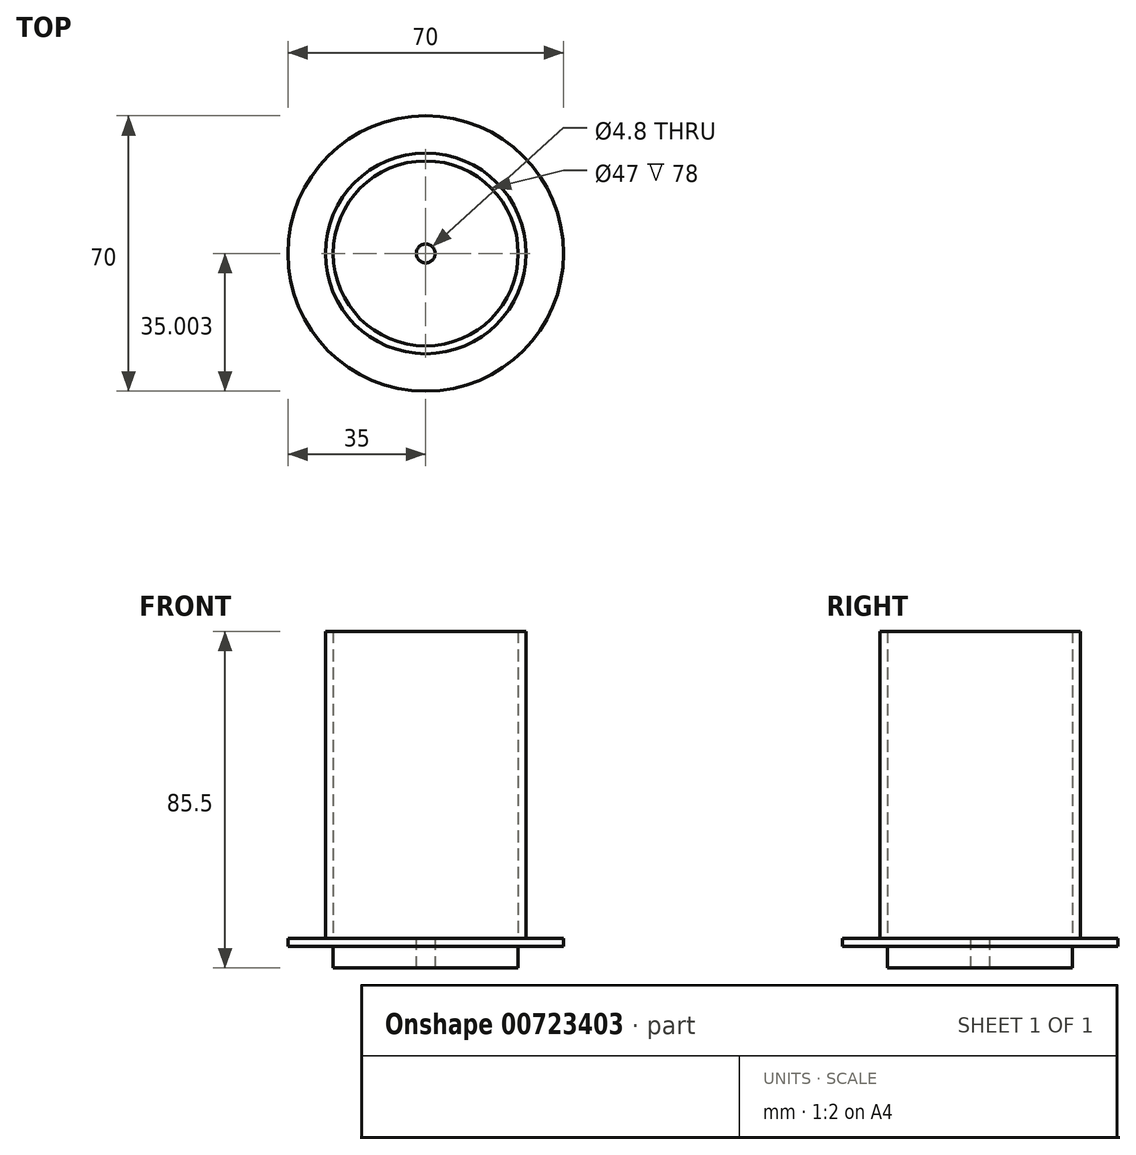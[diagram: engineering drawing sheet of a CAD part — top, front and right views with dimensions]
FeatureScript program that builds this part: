
annotation { "Feature Type Name" : "Feature", "Feature Type Description" : "" }
export const myFeature = defineFeature(function(context is Context, id is Id, definition is map)
    precondition{}
    {
        {
            var Q0;
            Q0=qCreatedBy(makeId("Top.planeOp"),FACE);
            var sketch = newSketch(context, id + "F0", { "sketchPlane" : qUnion([Q0])});
            skArc(sketch, "E0", {"start": v(20.08, -12.5) * mm, "mid": v(24.36, 1.65) * mm, "end": v(20.08, 15.8) * mm});
            skLineSegment(sketch, "E1.left", {"start": v(-10.34, -1.25) * mm, "end": v(-10.34, 4.55) * mm});
            skLineSegment(sketch, "E1.right", {"start": v(-5.54, -0.85) * mm, "end": v(-5.54, 4.15) * mm});
            skLineSegment(sketch, "E2", {"start": v(-10.34, 4.55) * mm, "end": v(-8.34, 4.55) * mm});
            skLineSegment(sketch, "E3", {"start": v(-8.34, 4.55) * mm, "end": v(-8.34, 6.55) * mm});
            skLineSegment(sketch, "E4", {"start": v(-8.34, 6.55) * mm, "end": v(-7.34, 6.55) * mm});
            skLineSegment(sketch, "E5", {"start": v(-7.34, 6.55) * mm, "end": v(-5.54, 4.15) * mm});
            skLineSegment(sketch, "E6", {"start": v(-10.34, -1.25) * mm, "end": v(-8.34, -1.25) * mm});
            skLineSegment(sketch, "E7", {"start": v(-8.34, -1.25) * mm, "end": v(-8.34, -3.25) * mm});
            skLineSegment(sketch, "E8", {"start": v(-8.34, -3.25) * mm, "end": v(-7.34, -3.25) * mm});
            skLineSegment(sketch, "E9", {"start": v(-7.34, -3.25) * mm, "end": v(-5.54, -0.85) * mm});
            skCircle(sketch, "E10", {"center": v(-1.14, 1.65) * mm, "radius": 35 * mm});
            skArc(sketch, "E11.0", {"start": v(18.63, -11.05) * mm, "mid": v(22.36, 1.65) * mm, "end": v(18.63, 14.35) * mm});
            skLineSegment(sketch, "E12.bottom", {"start": v(-15.29, 22.87) * mm, "end": v(-13.84, 21.42) * mm});
            skLineSegment(sketch, "E12.top", {"start": v(-22.36, 15.8) * mm, "end": v(-20.91, 14.35) * mm});
            skLineSegment(sketch, "E13.MirrorCS", {"start": v(20.08, 15.8) * mm, "end": v(18.63, 14.35) * mm});
            skLineSegment(sketch, "E14.MirrorCS", {"start": v(13, 22.87) * mm, "end": v(11.56, 21.42) * mm});
            skLineSegment(sketch, "E15.trimOffspring", {"start": v(11.56, -18.12) * mm, "end": v(13, -19.56) * mm});
            skLineSegment(sketch, "E16.trimOffspring", {"start": v(-13.84, -18.12) * mm, "end": v(-15.29, -19.56) * mm});
            skLineSegment(sketch, "E17.trimOffspring", {"start": v(-20.91, -11.05) * mm, "end": v(-22.36, -12.5) * mm});
            skLineSegment(sketch, "E18.trimOffspring", {"start": v(18.63, -11.05) * mm, "end": v(20.08, -12.5) * mm});
            skArc(sketch, "E19.trimOffspring", {"start": v(13, 22.87) * mm, "mid": v(-1.14, 27.15) * mm, "end": v(-15.29, 22.87) * mm});
            skArc(sketch, "E20.trimOffspring", {"start": v(11.56, 21.42) * mm, "mid": v(-1.14, 25.15) * mm, "end": v(-13.84, 21.42) * mm});
            skArc(sketch, "E21.trimOffspring", {"start": v(-20.91, 14.35) * mm, "mid": v(-24.64, 1.65) * mm, "end": v(-20.91, -11.05) * mm});
            skArc(sketch, "E22.trimOffspring", {"start": v(-22.36, 15.8) * mm, "mid": v(-26.64, 1.65) * mm, "end": v(-22.36, -12.5) * mm});
            skArc(sketch, "E23.trimOffspring", {"start": v(-13.84, -18.12) * mm, "mid": v(-1.14, -21.85) * mm, "end": v(11.56, -18.12) * mm});
            skArc(sketch, "E24.trimOffspring", {"start": v(-15.29, -19.56) * mm, "mid": v(-1.14, -23.85) * mm, "end": v(13, -19.56) * mm});
            skLineSegment(sketch, "E25.MirrorCS", {"start": v(3.26, -0.85) * mm, "end": v(3.26, 4.15) * mm});
            skLineSegment(sketch, "E26.MirrorCS", {"start": v(5.06, 6.55) * mm, "end": v(3.26, 4.15) * mm});
            skLineSegment(sketch, "E27.MirrorCS", {"start": v(6.06, 6.55) * mm, "end": v(5.06, 6.55) * mm});
            skLineSegment(sketch, "E28.MirrorCS", {"start": v(6.06, 4.55) * mm, "end": v(6.06, 6.55) * mm});
            skLineSegment(sketch, "E29.MirrorCS", {"start": v(8.06, 4.55) * mm, "end": v(6.06, 4.55) * mm});
            skLineSegment(sketch, "E30.MirrorCS", {"start": v(8.06, -1.25) * mm, "end": v(8.06, 4.55) * mm});
            skLineSegment(sketch, "E31.MirrorCS", {"start": v(8.06, -1.25) * mm, "end": v(6.06, -1.25) * mm});
            skLineSegment(sketch, "E32.MirrorCS", {"start": v(6.06, -1.25) * mm, "end": v(6.06, -3.25) * mm});
            skLineSegment(sketch, "E33.MirrorCS", {"start": v(6.06, -3.25) * mm, "end": v(5.06, -3.25) * mm});
            skLineSegment(sketch, "E34.MirrorCS", {"start": v(5.06, -3.25) * mm, "end": v(3.26, -0.85) * mm});
            skLineSegment(sketch, "E35.0", {"start": v(-55.8, 19.45) * mm, "end": v(-55.8, 19.45) * mm});
            skLineSegment(sketch, "E36.MirrorCS", {"start": v(1.76, -7.55) * mm, "end": v(1.76, -5.55) * mm});
            skLineSegment(sketch, "E37.MirrorCS", {"start": v(-6.04, -5.55) * mm, "end": v(-6.04, -4.55) * mm});
            skLineSegment(sketch, "E38.MirrorCS", {"start": v(-4.04, -7.55) * mm, "end": v(-4.04, -5.55) * mm});
            skLineSegment(sketch, "E39.MirrorCS", {"start": v(3.76, -5.55) * mm, "end": v(3.76, -4.55) * mm});
            skLineSegment(sketch, "E40.MirrorCS", {"start": v(3.76, -4.55) * mm, "end": v(1.36, -2.75) * mm});
            skLineSegment(sketch, "E41.MirrorCS", {"start": v(1.76, -5.55) * mm, "end": v(3.76, -5.55) * mm});
            skLineSegment(sketch, "E42.MirrorCS", {"start": v(-4.04, -5.55) * mm, "end": v(-6.04, -5.55) * mm});
            skLineSegment(sketch, "E43.MirrorCS", {"start": v(1.76, -7.55) * mm, "end": v(-4.04, -7.55) * mm});
            skLineSegment(sketch, "E44.MirrorCS", {"start": v(1.36, -2.75) * mm, "end": v(-3.64, -2.75) * mm});
            skLineSegment(sketch, "E45.MirrorCS", {"start": v(-6.04, -4.55) * mm, "end": v(-3.64, -2.75) * mm});
            skLineSegment(sketch, "E46.MirrorCS", {"start": v(3.76, 8.85) * mm, "end": v(3.76, 7.85) * mm});
            skLineSegment(sketch, "E47.MirrorCS", {"start": v(-4.04, 10.85) * mm, "end": v(-4.04, 8.85) * mm});
            skLineSegment(sketch, "E48.MirrorCS", {"start": v(-6.04, 7.85) * mm, "end": v(-3.64, 6.05) * mm});
            skLineSegment(sketch, "E49.MirrorCS", {"start": v(1.76, 10.85) * mm, "end": v(-4.04, 10.85) * mm});
            skLineSegment(sketch, "E50.MirrorCS", {"start": v(1.36, 6.05) * mm, "end": v(-3.64, 6.05) * mm});
            skLineSegment(sketch, "E51.MirrorCS", {"start": v(3.76, 7.85) * mm, "end": v(1.36, 6.05) * mm});
            skLineSegment(sketch, "E52.MirrorCS", {"start": v(1.76, 10.85) * mm, "end": v(1.76, 8.85) * mm});
            skLineSegment(sketch, "E53.MirrorCS", {"start": v(-4.04, 8.85) * mm, "end": v(-6.04, 8.85) * mm});
            skCircle(sketch, "E54.MirrorC", {"center": v(-1.14, 1.65) * mm, "radius": 2.4 * mm});
            skLineSegment(sketch, "E55.MirrorCS", {"start": v(-6.04, 8.85) * mm, "end": v(-6.04, 7.85) * mm});
            skLineSegment(sketch, "E56.MirrorCS", {"start": v(1.76, 8.85) * mm, "end": v(3.76, 8.85) * mm});
            skCircle(sketch, "E57", {"center": v(-1.14, 1.65) * mm, "radius": 25.5 * mm});
            skCircle(sketch, "E58", {"center": v(-1.14, 1.65) * mm, "radius": 23.5 * mm});
            skSolve(sketch);
        }
        {
            var Q0;
            {var subQ0=sQuery(id+"F0.wireOp",EDGE,"E13.MirrorCS");var subQ1=sQuery(id+"F0.wireOp",EDGE,"b31ca2aa-2784-4050-9d5b-8e0e7bdb5993");var subQ2=makeQuery(id+"F0.imprint","INTERSECT",VERTEX,{"derivedFrom":[subQ1,subQ0]});Q0=makeQuery(id+"F0.imprint","IMPRINT",FACE,{"disambiguationData":[TD([[makeQuery(id+"F0.imprint","IMPRINT",EDGE,{"disambiguationData":[TD([[subQ2,-1.0]])],"derivedFrom":subQ1}),1.0]])]});}
            var Q1;
            {var subQ0=sQuery(id+"F0.wireOp",EDGE,"FFj5b79C-maeM-itDx-LCIQ-9EkjaF8eI6C0");var subQ1=sQuery(id+"F0.wireOp",EDGE,"b31ca2aa-2784-4050-9d5b-8e0e7bdb5993");var subQ2=makeQuery(id+"F0.imprint","INTERSECT",VERTEX,{"derivedFrom":[subQ1,subQ0]});Q1=makeQuery(id+"F0.imprint","IMPRINT",FACE,{"disambiguationData":[TD([[makeQuery(id+"F0.imprint","IMPRINT",EDGE,{"disambiguationData":[TD([[subQ2,-1.0]])],"derivedFrom":subQ1}),1.0]])]});}
            var Q2;
            {var subQ0=sQuery(id+"F0.wireOp",EDGE,"E12.bottom");var subQ1=sQuery(id+"F0.wireOp",EDGE,"4563efc5-fb10-4338-9f63-69859ae92ad2.left");var subQ2=makeQuery(id+"F0.imprint","INTERSECT",VERTEX,{"derivedFrom":[subQ1,subQ0]});Q2=makeQuery(id+"F0.imprint","IMPRINT",FACE,{"disambiguationData":[TD([[makeQuery(id+"F0.imprint","IMPRINT",EDGE,{"disambiguationData":[TD([[subQ2,-1.0]])],"derivedFrom":subQ1}),1.0]])]});}
            var Q3;
            {var subQ0=sQuery(id+"F0.wireOp",EDGE,"FFj5b79C-maeM-itDx-LCIQ-9EkjaF8eI6C0");var subQ1=sQuery(id+"F0.wireOp",EDGE,"883a233e-beca-4438-a1aa-b8085ab23587");var subQ2=makeQuery(id+"F0.imprint","INTERSECT",VERTEX,{"disambiguationData":[OD(0.0)],"derivedFrom":[subQ1,subQ0]});Q3=makeQuery(id+"F0.imprint","IMPRINT",FACE,{"disambiguationData":[TD([[makeQuery(id+"F0.imprint","IMPRINT",EDGE,{"disambiguationData":[TD([[subQ2,1.0]])],"derivedFrom":subQ1}),1.0]])]});}
            var Q4;
            {var subQ0=sQuery(id+"F0.wireOp",EDGE,"FFj5b79C-maeM-itDx-LCIQ-9EkjaF8eI6C0");var subQ1=sQuery(id+"F0.wireOp",EDGE,"883a233e-beca-4438-a1aa-b8085ab23587");var subQ2=makeQuery(id+"F0.imprint","INTERSECT",VERTEX,{"disambiguationData":[OD(0.0)],"derivedFrom":[subQ1,subQ0]});Q4=makeQuery(id+"F0.imprint","IMPRINT",FACE,{"disambiguationData":[TD([[makeQuery(id+"F0.imprint","IMPRINT",EDGE,{"disambiguationData":[TD([[subQ2,-1.0]])],"derivedFrom":subQ1}),1.0]])]});}
            var Q5;
            {var subQ0=sQuery(id+"F0.wireOp",EDGE,"E14.MirrorCS");var subQ1=sQuery(id+"F0.wireOp",EDGE,"8299fe55-dfc4-4fbd-951d-2155e93de8ba");var subQ2=makeQuery(id+"F0.imprint","INTERSECT",VERTEX,{"derivedFrom":[subQ1,subQ0]});Q5=makeQuery(id+"F0.imprint","IMPRINT",FACE,{"disambiguationData":[TD([[makeQuery(id+"F0.imprint","IMPRINT",EDGE,{"disambiguationData":[TD([[subQ2,-1.0]])],"derivedFrom":subQ1}),1.0]])]});}
            var Q6;
            {var subQ0=sQuery(id+"F0.wireOp",EDGE,"FFj5b79C-maeM-itDx-LCIQ-9EkjaF8eI6C0");var subQ1=sQuery(id+"F0.wireOp",EDGE,"8299fe55-dfc4-4fbd-951d-2155e93de8ba");var subQ2=makeQuery(id+"F0.imprint","INTERSECT",VERTEX,{"derivedFrom":[subQ1,subQ0]});Q6=makeQuery(id+"F0.imprint","IMPRINT",FACE,{"disambiguationData":[TD([[makeQuery(id+"F0.imprint","IMPRINT",EDGE,{"disambiguationData":[TD([[subQ2,-1.0]])],"derivedFrom":subQ1}),1.0]])]});}
            var Q7;
            {var subQ0=sQuery(id+"F0.wireOp",EDGE,"E13.MirrorCS");var subQ1=sQuery(id+"F0.wireOp",EDGE,"E0");var subQ2=makeQuery(id+"F0.imprint","INTERSECT",VERTEX,{"disambiguationData":[OD(0.0)],"derivedFrom":[subQ1,subQ0]});Q7=makeQuery(id+"F0.imprint","IMPRINT",FACE,{"disambiguationData":[TD([[makeQuery(id+"F0.imprint","IMPRINT",EDGE,{"disambiguationData":[TD([[subQ2,-1.0]])],"derivedFrom":subQ1}),-1.0]])]});}
            var Q8;
            {var subQ0=sQuery(id+"F0.wireOp",EDGE,"E12.bottom");var subQ1=sQuery(id+"F0.wireOp",EDGE,"E0");var subQ2=makeQuery(id+"F0.imprint","INTERSECT",VERTEX,{"disambiguationData":[OD(0.0)],"derivedFrom":[subQ1,subQ0]});Q8=makeQuery(id+"F0.imprint","IMPRINT",FACE,{"disambiguationData":[TD([[makeQuery(id+"F0.imprint","IMPRINT",EDGE,{"disambiguationData":[TD([[subQ2,-1.0]])],"derivedFrom":subQ1}),-1.0]])]});}
            var Q9;
            {var subQ0=sQuery(id+"F0.wireOp",EDGE,"E12.top");var subQ1=sQuery(id+"F0.wireOp",EDGE,"E0");var subQ2=makeQuery(id+"F0.imprint","INTERSECT",VERTEX,{"disambiguationData":[OD(0.0)],"derivedFrom":[subQ1,subQ0]});Q9=makeQuery(id+"F0.imprint","IMPRINT",FACE,{"disambiguationData":[TD([[makeQuery(id+"F0.imprint","IMPRINT",EDGE,{"disambiguationData":[TD([[subQ2,-1.0]])],"derivedFrom":subQ1}),-1.0]])]});}
            var Q10;
            {var subQ0=sQuery(id+"F0.wireOp",EDGE,"E14.MirrorCS");var subQ1=sQuery(id+"F0.wireOp",EDGE,"E0");var subQ2=makeQuery(id+"F0.imprint","INTERSECT",VERTEX,{"disambiguationData":[OD(1.0)],"derivedFrom":[subQ1,subQ0]});Q10=makeQuery(id+"F0.imprint","IMPRINT",FACE,{"disambiguationData":[TD([[makeQuery(id+"F0.imprint","IMPRINT",EDGE,{"disambiguationData":[TD([[subQ2,-1.0]])],"derivedFrom":subQ1}),-1.0]])]});}
            var Q11;
            {var subQ0=sQuery(id+"F0.wireOp",EDGE,"E12.top");var subQ1=sQuery(id+"F0.wireOp",EDGE,"E0");var subQ2=makeQuery(id+"F0.imprint","INTERSECT",VERTEX,{"disambiguationData":[OD(1.0)],"derivedFrom":[subQ1,subQ0]});Q11=makeQuery(id+"F0.imprint","IMPRINT",FACE,{"disambiguationData":[TD([[makeQuery(id+"F0.imprint","IMPRINT",EDGE,{"disambiguationData":[TD([[subQ2,-1.0]])],"derivedFrom":subQ1}),-1.0]])]});}
            var Q12;
            {var subQ3=sQuery(id+"F0.wireOp",EDGE,"FFj5b79C-maeM-itDx-LCIQ-9EkjaF8eI6C0");var subQ5=sQuery(id+"F0.wireOp",EDGE,"883a233e-beca-4438-a1aa-b8085ab23587");var subQ14=makeQuery(id+"F0.imprint","INTERSECT",VERTEX,{"disambiguationData":[OD(0.0)],"derivedFrom":[subQ5,subQ3]});Q12=makeQuery(id+"F0.imprint","IMPRINT",FACE,{"disambiguationData":[TD([[makeQuery(id+"F0.imprint","IMPRINT",EDGE,{"disambiguationData":[TD([[subQ14,-1.0]])],"derivedFrom":subQ5}),-1.0]])]});}
            var Q13;
            {var subQ0=sQuery(id+"F0.wireOp",EDGE,"E14.MirrorCS");var subQ1=sQuery(id+"F0.wireOp",EDGE,"E1.left");var subQ2=makeQuery(id+"F0.imprint","INTERSECT",VERTEX,{"derivedFrom":[subQ1,subQ0]});Q13=makeQuery(id+"F0.imprint","IMPRINT",FACE,{"disambiguationData":[TD([[makeQuery(id+"F0.imprint","IMPRINT",EDGE,{"disambiguationData":[TD([[subQ2,-1.0]])],"derivedFrom":subQ1}),-1.0]])]});}
            var Q14;
            {var subQ0=sQuery(id+"F0.wireOp",EDGE,"b31ca2aa-2784-4050-9d5b-8e0e7bdb5993");var subQ1=sQuery(id+"F0.wireOp",EDGE,"3d37a358-cee8-4c43-93cd-1c7ba6a57ada.right");var subQ2=makeQuery(id+"F0.imprint","INTERSECT",VERTEX,{"derivedFrom":[subQ1,subQ0]});Q14=makeQuery(id+"F0.imprint","IMPRINT",FACE,{"disambiguationData":[TD([[makeQuery(id+"F0.imprint","IMPRINT",EDGE,{"disambiguationData":[TD([[subQ2,1.0]])],"derivedFrom":subQ1}),1.0]])]});}
            var Q15;
            {var subQ5=sQuery(id+"F0.wireOp",EDGE,"E1.right");Q15=makeQuery(id+"F0.imprint","IMPRINT",FACE,{"disambiguationData":[TD([[makeQuery(id+"F0.imprint","IMPRINT",EDGE,{"derivedFrom":subQ5}),-1.0]])]});}
            var Q16;
            {var subQ0=sQuery(id+"F0.wireOp",EDGE,"E14.MirrorCS");var subQ1=sQuery(id+"F0.wireOp",EDGE,"c0543988-83d3-4293-91c7-c859f428bb4d.trimOffspring");var subQ2=makeQuery(id+"F0.imprint","INTERSECT",VERTEX,{"derivedFrom":[subQ1,subQ0]});Q16=makeQuery(id+"F0.imprint","IMPRINT",FACE,{"disambiguationData":[TD([[makeQuery(id+"F0.imprint","IMPRINT",EDGE,{"disambiguationData":[TD([[subQ2,-1.0]])],"derivedFrom":subQ1}),1.0]])]});}
            var Q17;
            {var subQ1=sQuery(id+"F0.wireOp",EDGE,"E6");Q17=makeQuery(id+"F0.imprint","IMPRINT",FACE,{"disambiguationData":[TD([[makeQuery(id+"F0.imprint","IMPRINT",EDGE,{"derivedFrom":subQ1}),1.0]])]});}
            var Q18;
            {var subQ0=sQuery(id+"F0.wireOp",EDGE,"4563efc5-fb10-4338-9f63-69859ae92ad2.left");var subQ1=sQuery(id+"F0.wireOp",EDGE,"4563efc5-fb10-4338-9f63-69859ae92ad2.bottom");var subQ2=makeQuery(id+"F0.imprint","INTERSECT",VERTEX,{"derivedFrom":[subQ1,subQ0]});Q18=makeQuery(id+"F0.imprint","IMPRINT",FACE,{"disambiguationData":[TD([[makeQuery(id+"F0.imprint","IMPRINT",EDGE,{"disambiguationData":[TD([[subQ2,-1.0]])],"derivedFrom":subQ1}),-1.0]])]});}
            var Q19;
            {var subQ0=sQuery(id+"F0.wireOp",EDGE,"ef4e5805-de91-4d44-808a-910c9e40971a.trimOffspring");var subQ1=sQuery(id+"F0.wireOp",EDGE,"8299fe55-dfc4-4fbd-951d-2155e93de8ba");var subQ2=makeQuery(id+"F0.imprint","INTERSECT",VERTEX,{"derivedFrom":[subQ1,subQ0]});Q19=makeQuery(id+"F0.imprint","IMPRINT",FACE,{"disambiguationData":[TD([[makeQuery(id+"F0.imprint","IMPRINT",EDGE,{"disambiguationData":[TD([[subQ2,-1.0]])],"derivedFrom":subQ1}),1.0]])]});}
            var Q20;
            {var subQ7=sQuery(id+"F0.wireOp",EDGE,"4563efc5-fb10-4338-9f63-69859ae92ad2.left");var subQ8=sQuery(id+"F0.wireOp",EDGE,"4563efc5-fb10-4338-9f63-69859ae92ad2.bottom");var subQ9=makeQuery(id+"F0.imprint","INTERSECT",VERTEX,{"derivedFrom":[subQ8,subQ7]});Q20=makeQuery(id+"F0.imprint","IMPRINT",FACE,{"disambiguationData":[TD([[makeQuery(id+"F0.imprint","IMPRINT",EDGE,{"disambiguationData":[TD([[subQ9,-1.0]])],"derivedFrom":subQ8}),1.0]])]});}
            var Q21;
            {var subQ0=sQuery(id+"F0.wireOp",EDGE,"b31ca2aa-2784-4050-9d5b-8e0e7bdb5993");var subQ1=sQuery(id+"F0.wireOp",EDGE,"3d37a358-cee8-4c43-93cd-1c7ba6a57ada.left");var subQ2=makeQuery(id+"F0.imprint","INTERSECT",VERTEX,{"derivedFrom":[subQ1,subQ0]});Q21=makeQuery(id+"F0.imprint","IMPRINT",FACE,{"disambiguationData":[TD([[makeQuery(id+"F0.imprint","IMPRINT",EDGE,{"disambiguationData":[TD([[subQ2,1.0]])],"derivedFrom":subQ1}),-1.0]])]});}
            var Q22;
            {var subQ0=sQuery(id+"F0.wireOp",EDGE,"E11.0");var subQ1=sQuery(id+"F0.wireOp",EDGE,"3d37a358-cee8-4c43-93cd-1c7ba6a57ada.left");var subQ2=makeQuery(id+"F0.imprint","INTERSECT",VERTEX,{"derivedFrom":[subQ1,subQ0]});Q22=makeQuery(id+"F0.imprint","IMPRINT",FACE,{"disambiguationData":[TD([[makeQuery(id+"F0.imprint","IMPRINT",EDGE,{"disambiguationData":[TD([[subQ2,-1.0]])],"derivedFrom":subQ1}),-1.0]])]});}
            var Q23;
            {var subQ13=sQuery(id+"F0.wireOp",EDGE,"E6");Q23=makeQuery(id+"F0.imprint","IMPRINT",FACE,{"disambiguationData":[TD([[makeQuery(id+"F0.imprint","IMPRINT",EDGE,{"derivedFrom":subQ13}),-1.0]])]});}
            var Q24;
            {var subQ5=sQuery(id+"F0.wireOp",EDGE,"4563efc5-fb10-4338-9f63-69859ae92ad2.left");var subQ6=sQuery(id+"F0.wireOp",EDGE,"4563efc5-fb10-4338-9f63-69859ae92ad2.top");var subQ7=makeQuery(id+"F0.imprint","INTERSECT",VERTEX,{"derivedFrom":[subQ6,subQ5]});Q24=makeQuery(id+"F0.imprint","IMPRINT",FACE,{"disambiguationData":[TD([[makeQuery(id+"F0.imprint","IMPRINT",EDGE,{"disambiguationData":[TD([[subQ7,-1.0]])],"derivedFrom":subQ6}),-1.0]])]});}
            var Q25;
            {var subQ0=sQuery(id+"F0.wireOp",EDGE,"E11.0");var subQ1=sQuery(id+"F0.wireOp",EDGE,"3d37a358-cee8-4c43-93cd-1c7ba6a57ada.right");var subQ2=makeQuery(id+"F0.imprint","INTERSECT",VERTEX,{"derivedFrom":[subQ1,subQ0]});Q25=makeQuery(id+"F0.imprint","IMPRINT",FACE,{"disambiguationData":[TD([[makeQuery(id+"F0.imprint","IMPRINT",EDGE,{"disambiguationData":[TD([[subQ2,-1.0]])],"derivedFrom":subQ1}),1.0]])]});}
            var Q26;
            {var subQ0=sQuery(id+"F0.wireOp",EDGE,"E14.MirrorCS");var subQ1=sQuery(id+"F0.wireOp",EDGE,"E1.left");var subQ2=makeQuery(id+"F0.imprint","INTERSECT",VERTEX,{"derivedFrom":[subQ1,subQ0]});Q26=makeQuery(id+"F0.imprint","IMPRINT",FACE,{"disambiguationData":[TD([[makeQuery(id+"F0.imprint","IMPRINT",EDGE,{"disambiguationData":[TD([[subQ2,-1.0]])],"derivedFrom":subQ1}),1.0]])]});}
            var Q27;
            {var subQ0=sQuery(id+"F0.wireOp",EDGE,"c0543988-83d3-4293-91c7-c859f428bb4d.trimOffspring");var subQ1=sQuery(id+"F0.wireOp",EDGE,"8299fe55-dfc4-4fbd-951d-2155e93de8ba");var subQ2=makeQuery(id+"F0.imprint","INTERSECT",VERTEX,{"derivedFrom":[subQ1,subQ0]});Q27=makeQuery(id+"F0.imprint","IMPRINT",FACE,{"disambiguationData":[TD([[makeQuery(id+"F0.imprint","IMPRINT",EDGE,{"disambiguationData":[TD([[subQ2,1.0]])],"derivedFrom":subQ1}),1.0]])]});}
            var Q28;
            {var subQ1=sQuery(id+"F0.wireOp",EDGE,"E2");Q28=makeQuery(id+"F0.imprint","IMPRINT",FACE,{"disambiguationData":[TD([[makeQuery(id+"F0.imprint","IMPRINT",EDGE,{"derivedFrom":subQ1}),-1.0]])]});}
            var Q29;
            {var subQ0=sQuery(id+"F0.wireOp",EDGE,"E12.bottom");var subQ1=sQuery(id+"F0.wireOp",EDGE,"ef4e5805-de91-4d44-808a-910c9e40971a.trimOffspring");var subQ2=makeQuery(id+"F0.imprint","INTERSECT",VERTEX,{"derivedFrom":[subQ1,subQ0]});Q29=makeQuery(id+"F0.imprint","IMPRINT",FACE,{"disambiguationData":[TD([[makeQuery(id+"F0.imprint","IMPRINT",EDGE,{"disambiguationData":[TD([[subQ2,-1.0]])],"derivedFrom":subQ1}),-1.0]])]});}
            var Q30;
            {var subQ16=sQuery(id+"F0.wireOp",EDGE,"E2");Q30=makeQuery(id+"F0.imprint","IMPRINT",FACE,{"disambiguationData":[TD([[makeQuery(id+"F0.imprint","IMPRINT",EDGE,{"derivedFrom":subQ16}),1.0]])]});}
            var Q31;
            {var subQ0=sQuery(id+"F0.wireOp",EDGE,"E0");var subQ1=makeQuery(id+"F0.imprint","INTERSECT",VERTEX,{"derivedFrom":[subQ0,sQuery(id+"F0.wireOp",EDGE,"3d37a358-cee8-4c43-93cd-1c7ba6a57ada.right")]});Q31=makeQuery(id+"F0.imprint","IMPRINT",FACE,{"disambiguationData":[TD([[makeQuery(id+"F0.imprint","IMPRINT",EDGE,{"disambiguationData":[TD([[subQ1,1.0]])],"derivedFrom":subQ0}),-1.0]])]});}
            var Q32;
            {var subQ0=sQuery(id+"F0.wireOp",EDGE,"E11.0");var subQ1=sQuery(id+"F0.wireOp",EDGE,"3d37a358-cee8-4c43-93cd-1c7ba6a57ada.right");var subQ2=makeQuery(id+"F0.imprint","INTERSECT",VERTEX,{"derivedFrom":[subQ1,subQ0]});Q32=makeQuery(id+"F0.imprint","IMPRINT",FACE,{"disambiguationData":[TD([[makeQuery(id+"F0.imprint","IMPRINT",EDGE,{"disambiguationData":[TD([[subQ2,-1.0]])],"derivedFrom":subQ1}),-1.0]])]});}
            var Q33;
            {var subQ0=sQuery(id+"F0.wireOp",EDGE,"4563efc5-fb10-4338-9f63-69859ae92ad2.left");var subQ1=sQuery(id+"F0.wireOp",EDGE,"4563efc5-fb10-4338-9f63-69859ae92ad2.top");var subQ2=makeQuery(id+"F0.imprint","INTERSECT",VERTEX,{"derivedFrom":[subQ1,subQ0]});Q33=makeQuery(id+"F0.imprint","IMPRINT",FACE,{"disambiguationData":[TD([[makeQuery(id+"F0.imprint","IMPRINT",EDGE,{"disambiguationData":[TD([[subQ2,-1.0]])],"derivedFrom":subQ1}),1.0]])]});}
            var Q34;
            {var subQ5=sQuery(id+"F0.wireOp",EDGE,"E0");var subQ6=makeQuery(id+"F0.imprint","INTERSECT",VERTEX,{"derivedFrom":[subQ5,sQuery(id+"F0.wireOp",EDGE,"c0543988-83d3-4293-91c7-c859f428bb4d.trimOffspring")]});Q34=makeQuery(id+"F0.imprint","IMPRINT",FACE,{"disambiguationData":[TD([[makeQuery(id+"F0.imprint","IMPRINT",EDGE,{"disambiguationData":[TD([[subQ6,1.0]])],"derivedFrom":subQ5}),-1.0]])]});}
            var Q35;
            {var subQ0=sQuery(id+"F0.wireOp",EDGE,"E12.bottom");var subQ1=sQuery(id+"F0.wireOp",EDGE,"4563efc5-fb10-4338-9f63-69859ae92ad2.top");var subQ2=makeQuery(id+"F0.imprint","INTERSECT",VERTEX,{"derivedFrom":[subQ1,subQ0]});Q35=makeQuery(id+"F0.imprint","IMPRINT",FACE,{"disambiguationData":[TD([[makeQuery(id+"F0.imprint","IMPRINT",EDGE,{"disambiguationData":[TD([[subQ2,-1.0]])],"derivedFrom":subQ1}),-1.0]])]});}
            var Q36;
            {var subQ0=sQuery(id+"F0.wireOp",EDGE,"E11.0");var subQ1=sQuery(id+"F0.wireOp",EDGE,"3d37a358-cee8-4c43-93cd-1c7ba6a57ada.left");var subQ2=makeQuery(id+"F0.imprint","INTERSECT",VERTEX,{"derivedFrom":[subQ1,subQ0]});Q36=makeQuery(id+"F0.imprint","IMPRINT",FACE,{"disambiguationData":[TD([[makeQuery(id+"F0.imprint","IMPRINT",EDGE,{"disambiguationData":[TD([[subQ2,-1.0]])],"derivedFrom":subQ1}),1.0]])]});}
            var Q37;
            {var subQ3=sQuery(id+"F0.wireOp",EDGE,"E0");var subQ7=makeQuery(id+"F0.imprint","INTERSECT",VERTEX,{"derivedFrom":[subQ3,sQuery(id+"F0.wireOp",EDGE,"3d37a358-cee8-4c43-93cd-1c7ba6a57ada.left")]});Q37=makeQuery(id+"F0.imprint","IMPRINT",FACE,{"disambiguationData":[TD([[makeQuery(id+"F0.imprint","IMPRINT",EDGE,{"disambiguationData":[TD([[subQ7,1.0]])],"derivedFrom":subQ3}),-1.0]])]});}
            var Q38;
            {var subQ5=sQuery(id+"F0.wireOp",EDGE,"E0");var subQ8=makeQuery(id+"F0.imprint","INTERSECT",VERTEX,{"derivedFrom":[subQ5,sQuery(id+"F0.wireOp",EDGE,"4563efc5-fb10-4338-9f63-69859ae92ad2.bottom")]});Q38=makeQuery(id+"F0.imprint","IMPRINT",FACE,{"disambiguationData":[TD([[makeQuery(id+"F0.imprint","IMPRINT",EDGE,{"disambiguationData":[TD([[subQ8,-1.0]])],"derivedFrom":subQ5}),-1.0]])]});}
            var Q39;
            {var subQ5=sQuery(id+"F0.wireOp",EDGE,"E1.right");Q39=makeQuery(id+"F0.imprint","IMPRINT",FACE,{"disambiguationData":[TD([[makeQuery(id+"F0.imprint","IMPRINT",EDGE,{"derivedFrom":subQ5}),1.0]])]});}
            var Q40;
            {var subQ1=sQuery(id+"F0.wireOp",EDGE,"4563efc5-fb10-4338-9f63-69859ae92ad2.bottom");var subQ7=sQuery(id+"F0.wireOp",EDGE,"E13.MirrorCS");var subQ9=makeQuery(id+"F0.imprint","INTERSECT",VERTEX,{"derivedFrom":[subQ1,subQ7]});Q40=makeQuery(id+"F0.imprint","IMPRINT",FACE,{"disambiguationData":[TD([[makeQuery(id+"F0.imprint","IMPRINT",EDGE,{"disambiguationData":[TD([[subQ9,-1.0]])],"derivedFrom":subQ1}),-1.0]])]});}
            var Q41;
            {var subQ0=sQuery(id+"F0.wireOp",EDGE,"E14.MirrorCS");var subQ1=sQuery(id+"F0.wireOp",EDGE,"c0543988-83d3-4293-91c7-c859f428bb4d.trimOffspring");var subQ2=makeQuery(id+"F0.imprint","INTERSECT",VERTEX,{"derivedFrom":[subQ1,subQ0]});Q41=makeQuery(id+"F0.imprint","IMPRINT",FACE,{"disambiguationData":[TD([[makeQuery(id+"F0.imprint","IMPRINT",EDGE,{"disambiguationData":[TD([[subQ2,-1.0]])],"derivedFrom":subQ1}),-1.0]])]});}
            var Q42;
            {var subQ5=sQuery(id+"F0.wireOp",EDGE,"E0");var subQ7=makeQuery(id+"F0.imprint","INTERSECT",VERTEX,{"derivedFrom":[subQ5,sQuery(id+"F0.wireOp",EDGE,"ef4e5805-de91-4d44-808a-910c9e40971a.trimOffspring")]});Q42=makeQuery(id+"F0.imprint","IMPRINT",FACE,{"disambiguationData":[TD([[makeQuery(id+"F0.imprint","IMPRINT",EDGE,{"disambiguationData":[TD([[subQ7,1.0]])],"derivedFrom":subQ5}),-1.0]])]});}
            var Q43;
            {var subQ0=sQuery(id+"F0.wireOp",EDGE,"E12.bottom");var subQ1=sQuery(id+"F0.wireOp",EDGE,"ef4e5805-de91-4d44-808a-910c9e40971a.trimOffspring");var subQ2=makeQuery(id+"F0.imprint","INTERSECT",VERTEX,{"derivedFrom":[subQ1,subQ0]});Q43=makeQuery(id+"F0.imprint","IMPRINT",FACE,{"disambiguationData":[TD([[makeQuery(id+"F0.imprint","IMPRINT",EDGE,{"disambiguationData":[TD([[subQ2,-1.0]])],"derivedFrom":subQ1}),1.0]])]});}
            var Q44;
            {var subQ0=sQuery(id+"F0.wireOp",EDGE,"E13.MirrorCS");var subQ1=sQuery(id+"F0.wireOp",EDGE,"4563efc5-fb10-4338-9f63-69859ae92ad2.bottom");var subQ2=makeQuery(id+"F0.imprint","INTERSECT",VERTEX,{"derivedFrom":[subQ1,subQ0]});Q44=makeQuery(id+"F0.imprint","IMPRINT",FACE,{"disambiguationData":[TD([[makeQuery(id+"F0.imprint","IMPRINT",EDGE,{"disambiguationData":[TD([[subQ2,-1.0]])],"derivedFrom":subQ1}),1.0]])]});}
            var Q45;
            Q45=makeQuery(id+"F0.imprint","IMPRINT",FACE,{"disambiguationData":[TD([[makeQuery(id+"F0.imprint","IMPRINT",EDGE,{"derivedFrom":sQuery(id+"F0.wireOp",EDGE,"883a233e-beca-4438-a1aa-b8085ab23587")}),1.0]])]});
            var Q46;
            Q46=makeQuery(id+"F0.imprint","IMPRINT",FACE,{"disambiguationData":[TD([[makeQuery(id+"F0.imprint","IMPRINT",EDGE,{"derivedFrom":sQuery(id+"F0.wireOp",EDGE,"E46.MirrorCS")}),-1.0]])]});
            var Q47;
            Q47=makeQuery(id+"F0.imprint","IMPRINT",FACE,{"disambiguationData":[TD([[makeQuery(id+"F0.imprint","IMPRINT",EDGE,{"derivedFrom":sQuery(id+"F0.wireOp",EDGE,"E25.MirrorCS")}),-1.0]])]});
            var Q48;
            Q48=makeQuery(id+"F0.imprint","IMPRINT",FACE,{"disambiguationData":[TD([[makeQuery(id+"F0.imprint","IMPRINT",EDGE,{"derivedFrom":sQuery(id+"F0.wireOp",EDGE,"E54.MirrorC")}),-1.0]])]});
            var Q49;
            Q49=makeQuery(id+"F0.imprint","IMPRINT",FACE,{"disambiguationData":[TD([[makeQuery(id+"F0.imprint","IMPRINT",EDGE,{"derivedFrom":sQuery(id+"F0.wireOp",EDGE,"E36.MirrorCS")}),1.0]])]});
            var Q50;
            Q50=makeQuery(id+"F0.imprint","IMPRINT",FACE,{"disambiguationData":[TD([[makeQuery(id+"F0.imprint","IMPRINT",EDGE,{"derivedFrom":sQuery(id+"F0.wireOp",EDGE,"E12.top")}),-1.0]])]});
            var Q51;
            Q51=makeQuery(id+"F0.imprint","IMPRINT",FACE,{"disambiguationData":[TD([[makeQuery(id+"F0.imprint","IMPRINT",EDGE,{"derivedFrom":sQuery(id+"F0.wireOp",EDGE,"E12.bottom")}),1.0]])]});
            var Q52;
            Q52=makeQuery(id+"F0.imprint","IMPRINT",FACE,{"disambiguationData":[TD([[makeQuery(id+"F0.imprint","IMPRINT",EDGE,{"derivedFrom":sQuery(id+"F0.wireOp",EDGE,"E0")}),1.0]])]});
            var Q53;
            Q53=makeQuery(id+"F0.imprint","IMPRINT",FACE,{"disambiguationData":[TD([[makeQuery(id+"F0.imprint","IMPRINT",EDGE,{"derivedFrom":sQuery(id+"F0.wireOp",EDGE,"E15.trimOffspring")}),-1.0]])]});
            var Q54;
            {var subQ0=sQuery(id+"F0.wireOp",EDGE,"E15.trimOffspring");Q54=makeQuery(id+"F0.imprint","IMPRINT",FACE,{"disambiguationData":[TD([[makeQuery(id+"F0.imprint","IMPRINT",EDGE,{"derivedFrom":subQ0}),1.0]])]});}
            var Q55;
            {var subQ0=sQuery(id+"F0.wireOp",EDGE,"E13.MirrorCS");Q55=makeQuery(id+"F0.imprint","IMPRINT",FACE,{"disambiguationData":[TD([[makeQuery(id+"F0.imprint","IMPRINT",EDGE,{"derivedFrom":subQ0}),1.0]])]});}
            var Q56;
            Q56=makeQuery(id+"F0.imprint","IMPRINT",FACE,{"disambiguationData":[TD([[makeQuery(id+"F0.imprint","IMPRINT",EDGE,{"derivedFrom":sQuery(id+"F0.wireOp",EDGE,"E10")}),1.0]])]});
            var Q57;
            {var subQ0=sQuery(id+"F0.wireOp",EDGE,"E13.MirrorCS");Q57=makeQuery(id+"F0.imprint","IMPRINT",FACE,{"disambiguationData":[TD([[makeQuery(id+"F0.imprint","IMPRINT",EDGE,{"derivedFrom":subQ0}),-1.0]])]});}
            var Q58;
            {var subQ0=sQuery(id+"F0.wireOp",EDGE,"E12.bottom");Q58=makeQuery(id+"F0.imprint","IMPRINT",FACE,{"disambiguationData":[TD([[makeQuery(id+"F0.imprint","IMPRINT",EDGE,{"derivedFrom":subQ0}),-1.0]])]});}
            var Q59;
            {var subQ0=sQuery(id+"F0.wireOp",EDGE,"E16.trimOffspring");Q59=makeQuery(id+"F0.imprint","IMPRINT",FACE,{"disambiguationData":[TD([[makeQuery(id+"F0.imprint","IMPRINT",EDGE,{"derivedFrom":subQ0}),-1.0]])]});}
            extrude(context, id + "F1", {"entities" : qUnion([Q0, Q1, Q2, Q3, Q4, Q5, Q6, Q7, Q8, Q9, Q10, Q11, Q12, Q13, Q14, Q15, Q16, Q17, Q18, Q19, Q20, Q21, Q22, Q23, Q24, Q25, Q26, Q27, Q28, Q29, Q30, Q31, Q32, Q33, Q34, Q35, Q36, Q37, Q38, Q39, Q40, Q41, Q42, Q43, Q44, Q45, Q46, Q47, Q48, Q49, Q50, Q51, Q52, Q53, Q54, Q55, Q56, Q57, Q58, Q59]), "depth" : 2 * mm, "offsetDistance" : 25 * mm});
        }
        {
            var Q0;
            Q0=makeQuery(id+"F0.imprint","IMPRINT",FACE,{"disambiguationData":[TD([[makeQuery(id+"F0.imprint","IMPRINT",EDGE,{"derivedFrom":sQuery(id+"F0.wireOp",EDGE,"E12.bottom")}),1.0]])]});
            var Q1;
            Q1=makeQuery(id+"F0.imprint","IMPRINT",FACE,{"disambiguationData":[TD([[makeQuery(id+"F0.imprint","IMPRINT",EDGE,{"derivedFrom":sQuery(id+"F0.wireOp",EDGE,"E12.top")}),-1.0]])]});
            var Q2;
            Q2=makeQuery(id+"F0.imprint","IMPRINT",FACE,{"disambiguationData":[TD([[makeQuery(id+"F0.imprint","IMPRINT",EDGE,{"derivedFrom":sQuery(id+"F0.wireOp",EDGE,"E15.trimOffspring")}),-1.0]])]});
            var Q3;
            Q3=makeQuery(id+"F0.imprint","IMPRINT",FACE,{"disambiguationData":[TD([[makeQuery(id+"F0.imprint","IMPRINT",EDGE,{"derivedFrom":sQuery(id+"F0.wireOp",EDGE,"E0")}),1.0]])]});
            var Q4;
            {var subQ0=sQuery(id+"F0.wireOp",EDGE,"E13.MirrorCS");Q4=makeQuery(id+"F0.imprint","IMPRINT",FACE,{"disambiguationData":[TD([[makeQuery(id+"F0.imprint","IMPRINT",EDGE,{"derivedFrom":subQ0}),1.0]])]});}
            var Q5;
            {var subQ0=sQuery(id+"F0.wireOp",EDGE,"E15.trimOffspring");Q5=makeQuery(id+"F0.imprint","IMPRINT",FACE,{"disambiguationData":[TD([[makeQuery(id+"F0.imprint","IMPRINT",EDGE,{"derivedFrom":subQ0}),1.0]])]});}
            var Q6;
            {var subQ0=sQuery(id+"F0.wireOp",EDGE,"E13.MirrorCS");Q6=makeQuery(id+"F0.imprint","IMPRINT",FACE,{"disambiguationData":[TD([[makeQuery(id+"F0.imprint","IMPRINT",EDGE,{"derivedFrom":subQ0}),-1.0]])]});}
            var Q7;
            {var subQ0=sQuery(id+"F0.wireOp",EDGE,"E12.bottom");Q7=makeQuery(id+"F0.imprint","IMPRINT",FACE,{"disambiguationData":[TD([[makeQuery(id+"F0.imprint","IMPRINT",EDGE,{"derivedFrom":subQ0}),-1.0]])]});}
            var Q8;
            {var subQ0=sQuery(id+"F0.wireOp",EDGE,"E16.trimOffspring");Q8=makeQuery(id+"F0.imprint","IMPRINT",FACE,{"disambiguationData":[TD([[makeQuery(id+"F0.imprint","IMPRINT",EDGE,{"derivedFrom":subQ0}),-1.0]])]});}
            extrude(context, id + "F2", {"entities" : qUnion([Q0, Q1, Q2, Q3, Q4, Q5, Q6, Q7, Q8]), "operationType" : NewBodyOperationType.ADD, "depth" : 80 * mm, "offsetDistance" : 25 * mm});
        }
        {
            var Q0;
            Q0=makeQuery(id+"F0.imprint","IMPRINT",FACE,{"disambiguationData":[TD([[makeQuery(id+"F0.imprint","IMPRINT",EDGE,{"derivedFrom":sQuery(id+"F0.wireOp",EDGE,"E46.MirrorCS")}),-1.0]])]});
            var Q1;
            Q1=makeQuery(id+"F0.imprint","IMPRINT",FACE,{"disambiguationData":[TD([[makeQuery(id+"F0.imprint","IMPRINT",EDGE,{"derivedFrom":sQuery(id+"F0.wireOp",EDGE,"E1.left")}),-1.0]])]});
            var Q2;
            Q2=makeQuery(id+"F0.imprint","IMPRINT",FACE,{"disambiguationData":[TD([[makeQuery(id+"F0.imprint","IMPRINT",EDGE,{"derivedFrom":sQuery(id+"F0.wireOp",EDGE,"E54.MirrorC")}),-1.0]])]});
            var Q3;
            Q3=makeQuery(id+"F0.imprint","IMPRINT",FACE,{"disambiguationData":[TD([[makeQuery(id+"F0.imprint","IMPRINT",EDGE,{"derivedFrom":sQuery(id+"F0.wireOp",EDGE,"E25.MirrorCS")}),-1.0]])]});
            var Q4;
            Q4=makeQuery(id+"F0.imprint","IMPRINT",FACE,{"disambiguationData":[TD([[makeQuery(id+"F0.imprint","IMPRINT",EDGE,{"derivedFrom":sQuery(id+"F0.wireOp",EDGE,"E36.MirrorCS")}),1.0]])]});
            extrude(context, id + "F3", {"entities" : qUnion([Q0, Q1, Q2, Q3, Q4]), "operationType" : NewBodyOperationType.ADD, "oppositeDirection" : true, "depth" : 5.5 * mm, "offsetDistance" : 25 * mm});
        }
    });
